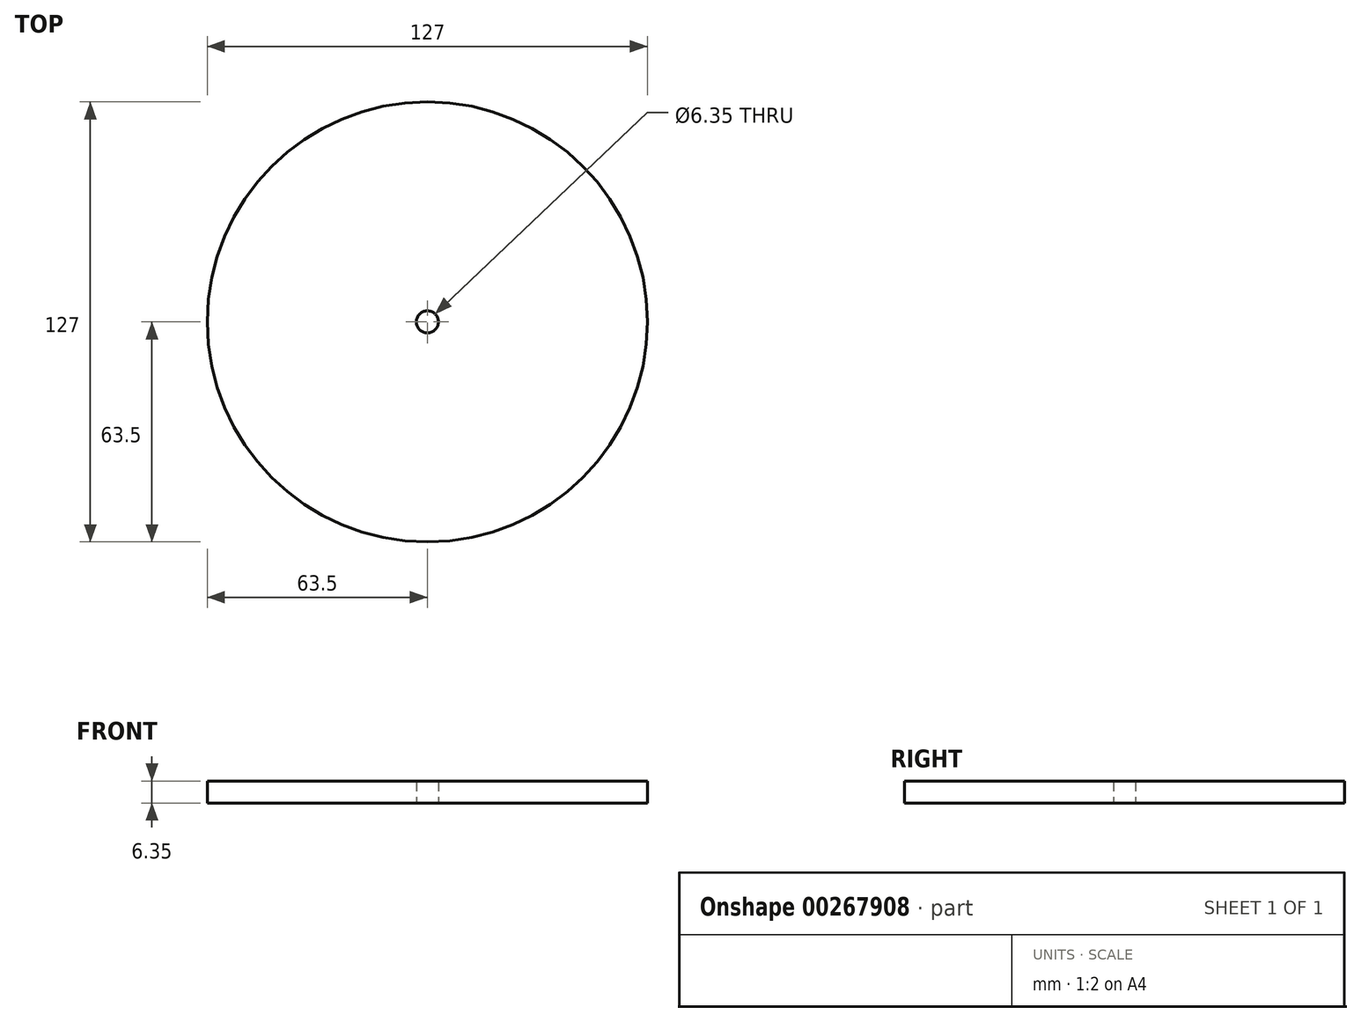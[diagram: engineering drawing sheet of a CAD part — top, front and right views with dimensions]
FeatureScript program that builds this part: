
annotation { "Feature Type Name" : "Feature", "Feature Type Description" : "" }
export const myFeature = defineFeature(function(context is Context, id is Id, definition is map)
    precondition{}
    {
        {
            var Q0;
            Q0=qCreatedBy(makeId("Top.planeOp"),FACE);
            var sketch = newSketch(context, id + "F0", { "sketchPlane" : qUnion([Q0])});
            skCircle(sketch, "E0", {"center": v(0, 0) * mm, "radius": 3.18 * mm});
            skCircle(sketch, "E1", {"center": v(0, 0) * mm, "radius": 63.5 * mm});
            skSolve(sketch);
        }
        {
            var Q0;
            Q0=qSketchRegion(id+"F0",true);
            extrude(context, id + "F1", {"entities" : qUnion([Q0]), "depth" : 6.35 * mm});
        }
    });
